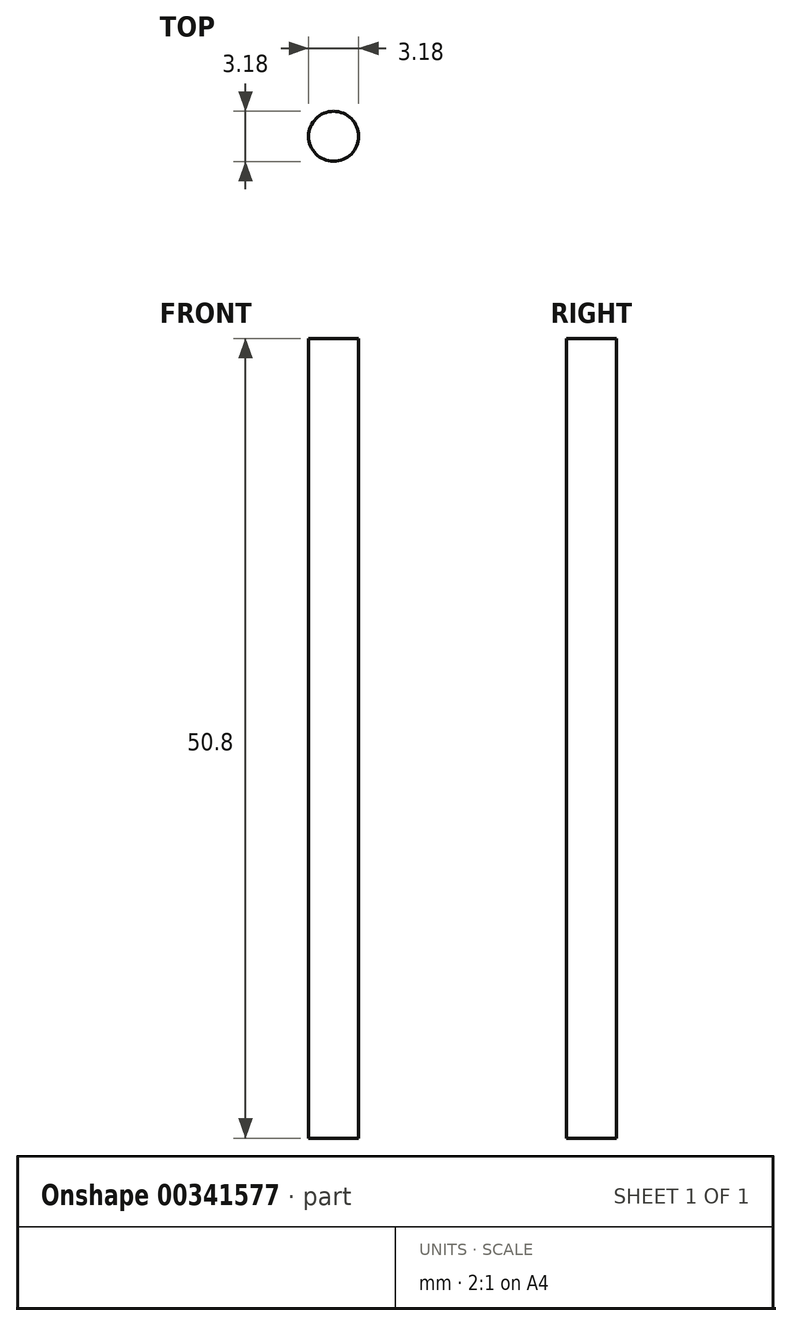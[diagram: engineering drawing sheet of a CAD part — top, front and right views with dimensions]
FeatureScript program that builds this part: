
annotation { "Feature Type Name" : "Feature", "Feature Type Description" : "" }
export const myFeature = defineFeature(function(context is Context, id is Id, definition is map)
    precondition{}
    {
        {
            var Q0;
            Q0=qCreatedBy(makeId("Top.planeOp"),FACE);
            var sketch = newSketch(context, id + "F0", { "sketchPlane" : qUnion([Q0])});
            skCircle(sketch, "E0", {"center": v(0, 0) * mm, "radius": 1.59 * mm});
            skSolve(sketch);
        }
        {
            var Q0;
            Q0 = qSketchRegion(id + "F0", true);
            extrude(context, id + "F1", {"entities" : qUnion([Q0]), "depth" : 50.8 * mm});
        }
    });
